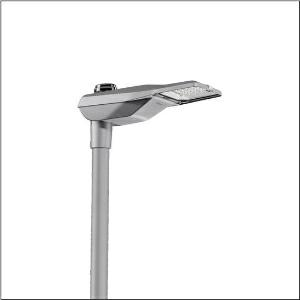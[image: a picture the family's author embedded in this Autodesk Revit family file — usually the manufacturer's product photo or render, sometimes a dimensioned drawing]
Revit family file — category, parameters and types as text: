
# Revit family: streetlight_sl_21_micro___st0_8a_5xe5c47n08db_8458
name_source: partatom
category: Lighting Fixtures
units: mm (PartAtom-declared; Revit-internal decimal feet)

## family parameters
Cut with Voids When Loaded = No
Host = Face
Light Source = No
Part Type = Normal
Room Calculation Point = No
Round Connector Dimension = Use Diameter
Shared = No

## types (1)
- --- (1 x LED, 5320 lm, 39.1 W, 4000K)
    Apparent Load = 39 VA
    CIE Flux Codes = 38 75 97 100 100
    Color Rendering = 70
    Color Temperature = 4000K
    Default Elevation = 1800 mm
    Description = Streetlight SL 21 micro, mast luminaire, primary light control with lens, of PMMA, primary optical cover: cover, of toughened safety glass, transparent, light distribution: ST0.8a, light emission: direct distribution, primary light characteristic: asymmetric, installation type: post-top, LED, 3G 1.5mm², High Power LED, rated luminous flux: 5.320lm, luminous efficacy: 136lm/W, light colour: 740, colour temperature: 4000K, control: overheat protection, presetting dimming linear, constant luminous flux control, time-dependent luminous flux control, flexible luminous flux parameterisation, mains connection: 230..240V, AC, 50/60Hz, connection cable pre-assembled, cable length: 6,5m, wiring characteristics: H07RN-F, start of lifetime: 39W, end of service life: 41W, reduction: 18W, luminaire housing, of diecast aluminium (EN AC-44300), powder-coated, Siteco® metallic grey (DB 702S), corrosivity category C5 mid according to DIN EN ISO 12944, multi-level sealing system, sealing non-destructively replaceable, inclination adjustable: 0°, 5°, 10°, 15°, length: 528mm, width: 235mm, height: 110mm, spigot size: 76/60mm (post-top), protection rating (complete): IP66, insulation class (complete): insulation class I (protective earthing), certification: CE, ENEC, ENEC+, VDE, impact resistance: IK09, permissible operating ambient temperature for outdoor applications: -40..+50°C, standard-compliant lighting for roads and squares, packaging unit: 1 piece

Light Distribution: ST0.8a
    Height = 110 mm
    Lamp = 1 x LED
    Lamp Light Flux = 5320 lm
    Lamp Power = 39.1 W
    Lamp count = 1
    Length = 528 mm
    Luminous efficacy = 136 lm/W
    Manufacturer = Siteco
    ModVariant = No
    Model = 5XE5C47N08DB
    Number of Poles = 1
    OnlyDefault = Yes
    Power Factor = 1
    Product Name = Streetlight SL 21 micro | ST0.8a
    Product group = mast luminaire | pylon top
    ProductGroupID = 6100
    Protection Class = Protection class I
    Protection Degree = IP 66
    RLX_Detail_Level = 1
    RLX_Emergency_Light_Flux = 0 lm
    RLX_Emergency_Type = 0
    RLX_Emergency_Type_DB = No
    RlxData = <blob elided: 98561 chars, md5=7c1c24bf>
    Socket = socket
    Standby Power = 0 W
    System Light Flux = 5320 lm
    System Power = 39 W
    Type Comments = factory setting: luminous flux: 100 % | dim-lin: 254 | 765 mA
    Type Image = l_1294375.jpg
    URL = http://relux.com
    VarID = @adj_083681
    Voltage = 0 V
    Weight = 0.00 kg
    Width = 235 mm

## geometry (parser evidence)
native form markers: Blend x4, Sweep x9
no freeform markers — native parametric forms only
